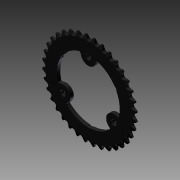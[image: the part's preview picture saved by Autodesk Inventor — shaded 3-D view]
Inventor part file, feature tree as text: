
AUTODESK INVENTOR PART (.ipt)
format: ipt  version: 2012 (Build 160160000, 160)  size: 1,181,184 bytes
history: native  units: in
note: dims shown in document units (in); Inventor stores cm internally (conversion verified against a paired STEP export)
features: boolean_combine x1, extrude x1, imported_body x1, sketch x1
ambient origin geometry x8: Origin, YZ Plane, XZ Plane, XY Plane, X Axis, Y Axis, Z Axis, Center Point
feature tree (4):
  boolean_combine  "Combine1"
  extrude  "Extrusion1"  [1 undecoded]
  imported_body  "Base1"
  sketch  "Sketch4"  dims[d1=0.0in d2=0.0in]
note: 1 required parameter value undecoded (feature->parameter linkage not recoverable at this tier; creation-order binding heuristic only, values carry confidence <= 0.55)
